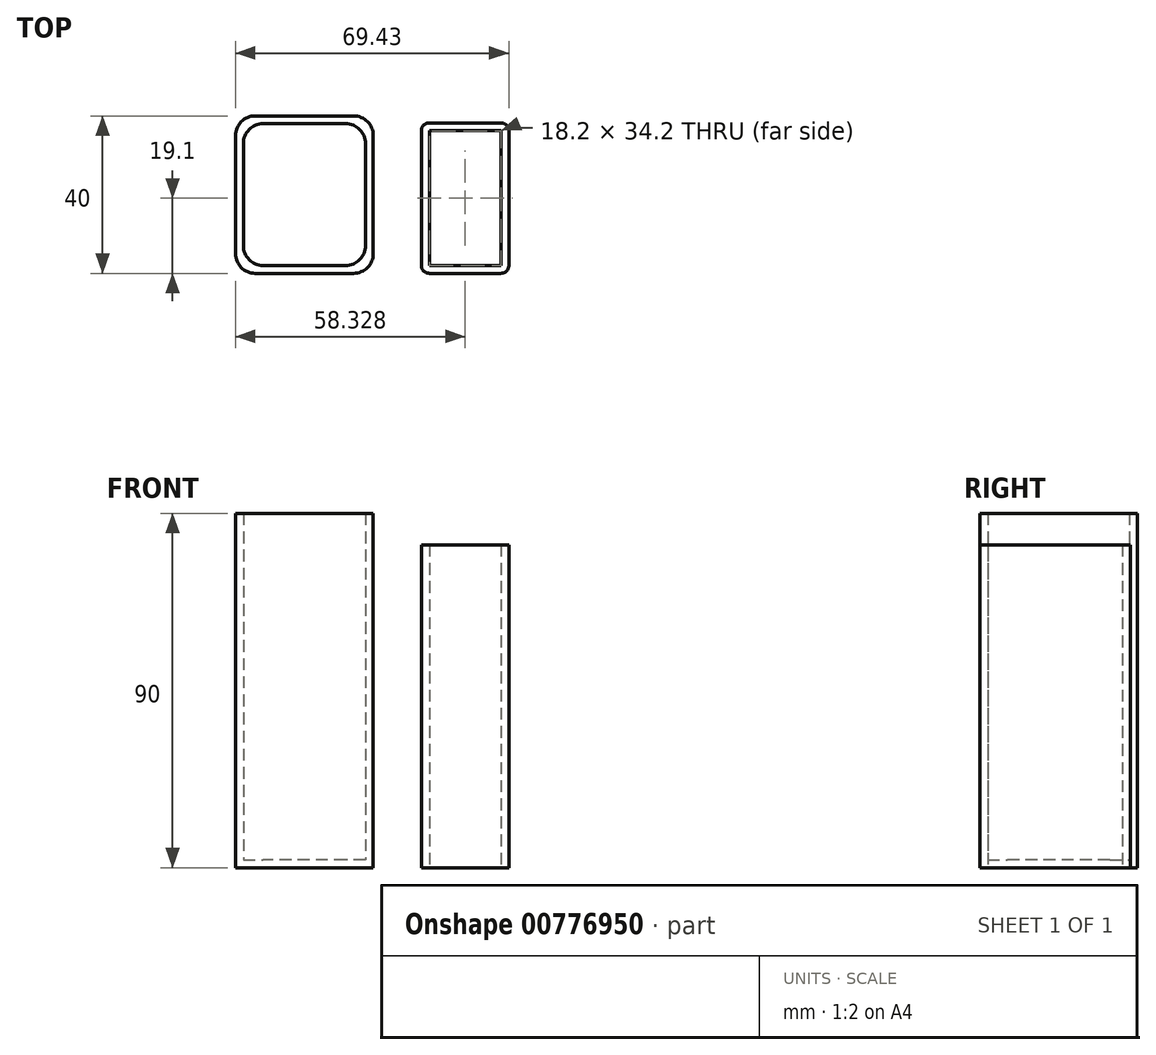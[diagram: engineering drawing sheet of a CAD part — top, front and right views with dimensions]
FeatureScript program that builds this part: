
annotation { "Feature Type Name" : "Feature", "Feature Type Description" : "" }
export const myFeature = defineFeature(function(context is Context, id is Id, definition is map)
    precondition{}
    {
        {
            var Q0;
            Q0=qCreatedBy(makeId("Top.planeOp"),FACE);
            var sketch = newSketch(context, id + "F0", { "sketchPlane" : qUnion([Q0])});
            skLineSegment(sketch, "E0.bottom", {"start": v(12.5, 20) * mm, "end": v(-12.5, 20) * mm});
            skLineSegment(sketch, "E0.top", {"start": v(12.5, -20) * mm, "end": v(-12.5, -20) * mm});
            skLineSegment(sketch, "E0.left", {"start": v(17.5, 15) * mm, "end": v(17.5, -15) * mm});
            skLineSegment(sketch, "E0.right", {"start": v(-17.5, 15) * mm, "end": v(-17.5, -15) * mm});
            skPoint(sketch, "E0.middle", {"position": v(0, 0) * mm});
            skPoint(sketch, "E1.visualSharp", {"position": v(-17.5, 20) * mm});
            skArc(sketch, "E1.filletArc", {"start": v(-12.5, 20) * mm, "mid": v(-16.04, 18.54) * mm, "end": v(-17.5, 15) * mm});
            skPoint(sketch, "E2.visualSharp", {"position": v(17.5, 20) * mm});
            skArc(sketch, "E2.filletArc", {"start": v(17.5, 15) * mm, "mid": v(16.04, 18.54) * mm, "end": v(12.5, 20) * mm});
            skPoint(sketch, "E3.visualSharp", {"position": v(17.5, -20) * mm});
            skArc(sketch, "E3.filletArc", {"start": v(12.5, -20) * mm, "mid": v(16.04, -18.54) * mm, "end": v(17.5, -15) * mm});
            skPoint(sketch, "E4.visualSharp", {"position": v(-17.5, -20) * mm});
            skArc(sketch, "E4.filletArc", {"start": v(-17.5, -15) * mm, "mid": v(-16.04, -18.54) * mm, "end": v(-12.5, -20) * mm});
            skLineSegment(sketch, "E5.0", {"start": v(-15.5, 13) * mm, "end": v(-15.5, -13) * mm});
            skLineSegment(sketch, "E6.0", {"start": v(10.5, 18) * mm, "end": v(-10.5, 18) * mm});
            skLineSegment(sketch, "E7.0", {"start": v(15.5, 13) * mm, "end": v(15.5, -13) * mm});
            skLineSegment(sketch, "E8.0", {"start": v(10.5, -18) * mm, "end": v(-10.5, -18) * mm});
            skPoint(sketch, "E9.visualSharp", {"position": v(-15.5, 18) * mm});
            skArc(sketch, "E9.filletArc", {"start": v(-10.5, 18) * mm, "mid": v(-14.04, 16.54) * mm, "end": v(-15.5, 13) * mm});
            skPoint(sketch, "E10.visualSharp", {"position": v(15.5, 18) * mm});
            skArc(sketch, "E10.filletArc", {"start": v(15.5, 13) * mm, "mid": v(14.04, 16.54) * mm, "end": v(10.5, 18) * mm});
            skPoint(sketch, "E11.visualSharp", {"position": v(15.5, -18) * mm});
            skArc(sketch, "E11.filletArc", {"start": v(10.5, -18) * mm, "mid": v(14.04, -16.54) * mm, "end": v(15.5, -13) * mm});
            skPoint(sketch, "E12.visualSharp", {"position": v(-15.5, -18) * mm});
            skArc(sketch, "E12.filletArc", {"start": v(-15.5, -13) * mm, "mid": v(-14.04, -16.54) * mm, "end": v(-10.5, -18) * mm});
            skSolve(sketch);
        }
        {
            var Q0;
            Q0=makeQuery(id+"F0.imprint","IMPRINT",FACE,{"disambiguationData":[TD([[makeQuery(id+"F0.imprint","IMPRINT",EDGE,{"derivedFrom":sQuery(id+"F0.wireOp",EDGE,"E0.bottom")}),1.0]])]});
            extrude(context, id + "F1", {"entities" : qUnion([Q0]), "depth" : 90 * mm, "offsetDistance" : 25 * mm});
        }
        {
            var Q0;
            Q0=makeQuery(id+"F0.imprint","IMPRINT",FACE,{"disambiguationData":[TD([[makeQuery(id+"F0.imprint","IMPRINT",EDGE,{"derivedFrom":sQuery(id+"F0.wireOp",EDGE,"E5.0")}),1.0]])]});
            extrude(context, id + "F2", {"entities" : qUnion([Q0]), "operationType" : NewBodyOperationType.ADD, "depth" : 2 * mm, "offsetDistance" : 25 * mm});
        }
        {
            var Q0;
            Q0=qCreatedBy(makeId("Top.planeOp"),FACE);
            var sketch = newSketch(context, id + "F3", { "sketchPlane" : qUnion([Q0])});
            skLineSegment(sketch, "E13.bottom", {"start": v(31.73, 18.2) * mm, "end": v(49.93, 18.2) * mm});
            skLineSegment(sketch, "E13.top", {"start": v(31.73, -20) * mm, "end": v(49.93, -20) * mm});
            skLineSegment(sketch, "E13.left", {"start": v(29.73, 16.2) * mm, "end": v(29.73, -18) * mm});
            skLineSegment(sketch, "E13.right", {"start": v(51.93, 16.2) * mm, "end": v(51.93, -18) * mm});
            skPoint(sketch, "E14.visualSharp", {"position": v(29.73, -20) * mm});
            skArc(sketch, "E14.filletArc", {"start": v(29.73, -18) * mm, "mid": v(30.31, -19.41) * mm, "end": v(31.73, -20) * mm});
            skPoint(sketch, "E15.visualSharp", {"position": v(51.93, -20) * mm});
            skArc(sketch, "E15.filletArc", {"start": v(49.93, -20) * mm, "mid": v(51.34, -19.41) * mm, "end": v(51.93, -18) * mm});
            skPoint(sketch, "E16.visualSharp", {"position": v(29.73, 18.2) * mm});
            skArc(sketch, "E16.filletArc", {"start": v(31.73, 18.2) * mm, "mid": v(30.31, 17.61) * mm, "end": v(29.73, 16.2) * mm});
            skPoint(sketch, "E17.visualSharp", {"position": v(51.93, 18.2) * mm});
            skArc(sketch, "E17.filletArc", {"start": v(51.93, 16.2) * mm, "mid": v(51.34, 17.61) * mm, "end": v(49.93, 18.2) * mm});
            skLineSegment(sketch, "E18.0", {"start": v(31.73, 16.2) * mm, "end": v(31.73, -18) * mm});
            skLineSegment(sketch, "E19.0", {"start": v(31.73, 16.2) * mm, "end": v(49.93, 16.2) * mm});
            skLineSegment(sketch, "E20.0", {"start": v(49.93, 16.2) * mm, "end": v(49.93, -18) * mm});
            skLineSegment(sketch, "E21.0", {"start": v(31.73, -18) * mm, "end": v(49.93, -18) * mm});
            skSolve(sketch);
        }
        {
            var Q0;
            Q0=makeQuery(id+"F3.imprint","IMPRINT",FACE,{"disambiguationData":[TD([[makeQuery(id+"F3.imprint","IMPRINT",EDGE,{"derivedFrom":sQuery(id+"F3.wireOp",EDGE,"E13.bottom")}),-1.0]])]});
            extrude(context, id + "F4", {"entities" : qUnion([Q0]), "depth" : 82 * mm, "offsetDistance" : 25 * mm});
        }
    });
